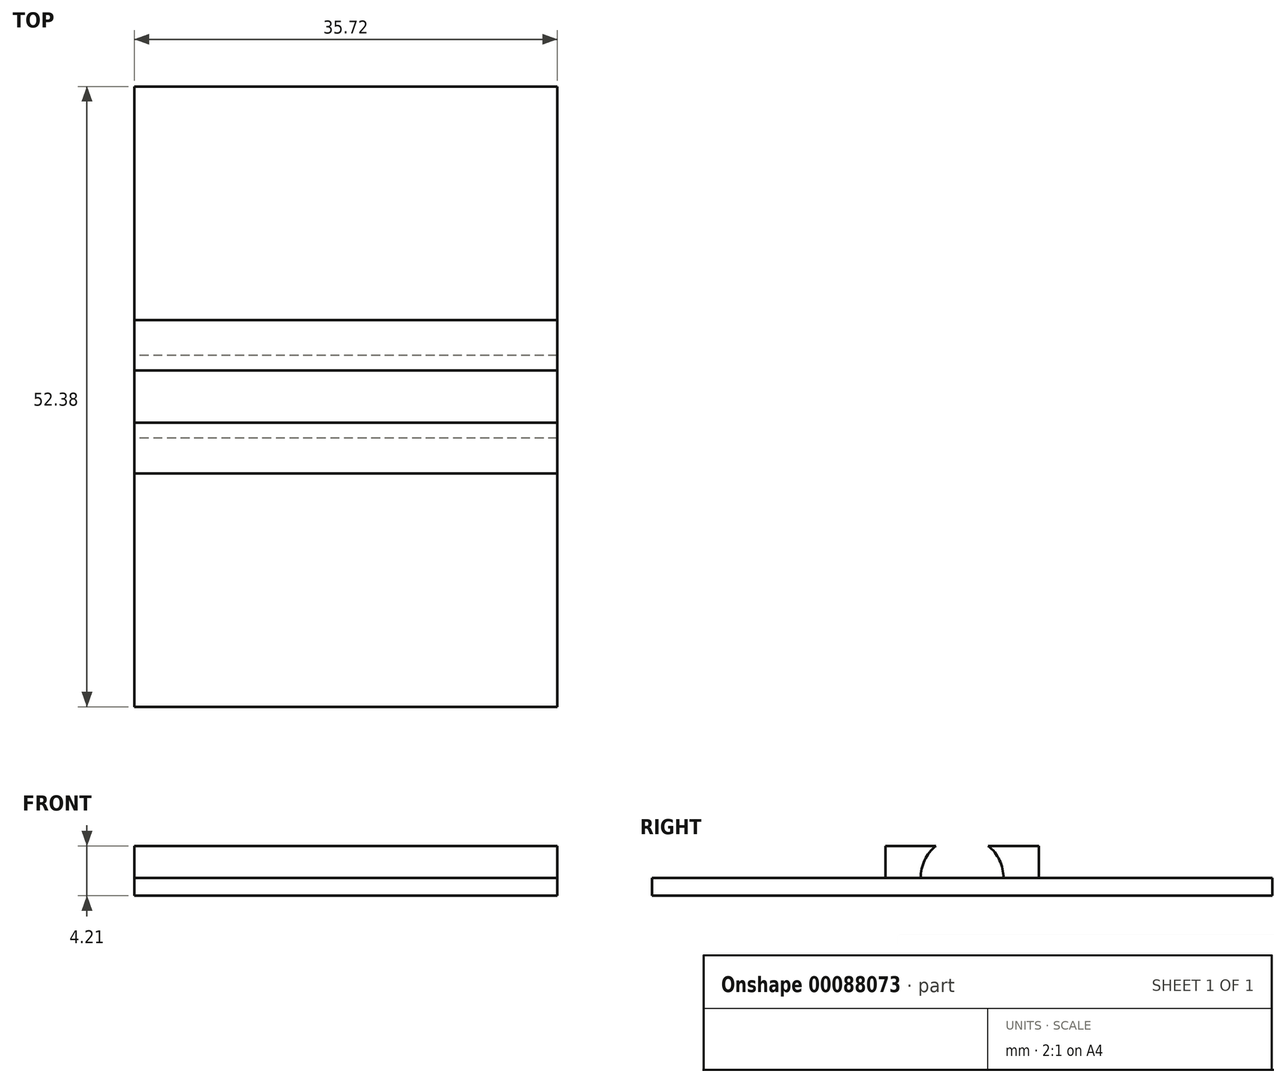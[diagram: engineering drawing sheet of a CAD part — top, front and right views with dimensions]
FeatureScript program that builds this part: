
annotation { "Feature Type Name" : "Feature", "Feature Type Description" : "" }
export const myFeature = defineFeature(function(context is Context, id is Id, definition is map)
    precondition{}
    {
        {
            var Q0;
            Q0=qCreatedBy(makeId("Top.planeOp"),FACE);
            var sketch = newSketch(context, id + "F0", { "sketchPlane" : qUnion([Q0])});
            skLineSegment(sketch, "E0.bottom", {"start": v(17.86, -26.19) * mm, "end": v(-17.86, -26.2) * mm});
            skLineSegment(sketch, "E0.top", {"start": v(17.86, 26.2) * mm, "end": v(-17.86, 26.2) * mm});
            skLineSegment(sketch, "E0.left", {"start": v(17.86, -26.19) * mm, "end": v(17.86, 26.2) * mm});
            skLineSegment(sketch, "E0.right", {"start": v(-17.86, -26.2) * mm, "end": v(-17.86, 26.2) * mm});
            skPoint(sketch, "E0.middle", {"position": v(0, 0) * mm});
            skSolve(sketch);
        }
        {
            var Q0;
            Q0 = qSketchRegion(id + "F0", true);
            extrude(context, id + "F1", {"entities" : qUnion([Q0]), "depth" : 1.5 * mm});
        }
        {
            var Q0;
            Q0=makeQuery(id+"F1.opExtrude","SWEPT_FACE",FACE,{"disambiguationData":[OSD([sQuery(id+"F0.wireOp",EDGE,"E0.right")])]});
            var sketch = newSketch(context, id + "F2", { "sketchPlane" : qUnion([Q0])});
            skArc(sketch, "E1", {"start": v(3.5, 1.5) * mm, "mid": v(0, 5) * mm, "end": v(-3.5, 1.5) * mm, "construction": true});
            skLineSegment(sketch, "E2", {"start": v(-2.2, 4.21) * mm, "end": v(-6.48, 4.21) * mm});
            skLineSegment(sketch, "E3", {"start": v(-6.48, 4.21) * mm, "end": v(-6.48, 1.5) * mm});
            skArc(sketch, "E4", {"start": v(-2.2, 4.21) * mm, "mid": v(-3.16, 3) * mm, "end": v(-3.5, 1.5) * mm});
            skArc(sketch, "E5.MirrorCS", {"start": v(2.2, 4.21) * mm, "mid": v(3.16, 3) * mm, "end": v(3.5, 1.5) * mm});
            skLineSegment(sketch, "E6.MirrorCS", {"start": v(2.2, 4.21) * mm, "end": v(6.48, 4.21) * mm});
            skLineSegment(sketch, "E7.MirrorCS", {"start": v(6.48, 4.21) * mm, "end": v(6.48, 1.5) * mm});
            skLineSegment(sketch, "E8", {"start": v(-6.48, 1.5) * mm, "end": v(-3.5, 1.5) * mm});
            skLineSegment(sketch, "E9", {"start": v(3.5, 1.5) * mm, "end": v(6.48, 1.5) * mm});
            skSolve(sketch);
        }
        {
            var Q0;
            Q0 = qSketchRegion(id + "F2", true);
            var Q1;
            Q1=makeQuery(id+"F1.opExtrude","SWEPT_FACE",FACE,{"disambiguationData":[OSD([sQuery(id+"F0.wireOp",EDGE,"E0.left")])]});
            extrude(context, id + "F3", {"entities" : qUnion([Q0]), "endBound" : BoundingType.UP_TO_SURFACE, "oppositeDirection" : true, "endBoundEntityFace" : qUnion([Q1]), "depth" : 25 * mm});
        }
    });
